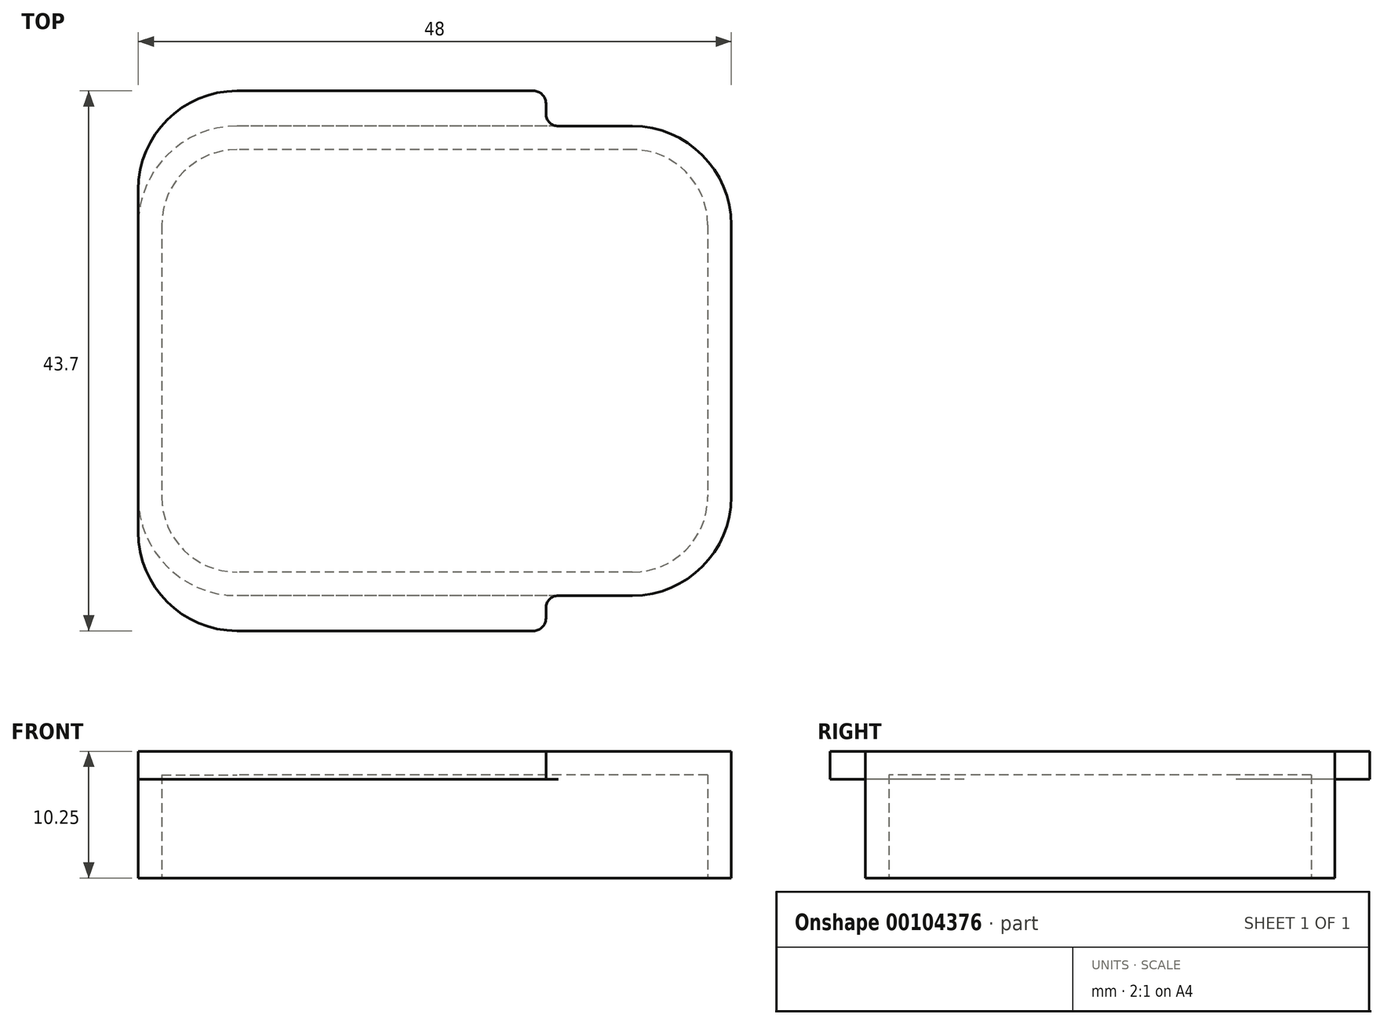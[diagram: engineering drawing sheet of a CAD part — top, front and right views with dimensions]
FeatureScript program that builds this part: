
annotation { "Feature Type Name" : "Feature", "Feature Type Description" : "" }
export const myFeature = defineFeature(function(context is Context, id is Id, definition is map)
    precondition{}
    {
        {
            var Q0;
            Q0=qCreatedBy(makeId("Top.planeOp"),FACE);
            var sketch = newSketch(context, id + "F0", { "sketchPlane" : qUnion([Q0])});
            skLineSegment(sketch, "E0.bottom", {"start": v(16, 19) * mm, "end": v(-16, 19) * mm});
            skLineSegment(sketch, "E0.top", {"start": v(16, -19) * mm, "end": v(-16, -19) * mm});
            skLineSegment(sketch, "E0.left", {"start": v(24, 11) * mm, "end": v(24, -11) * mm});
            skLineSegment(sketch, "E0.right", {"start": v(-24, 11) * mm, "end": v(-24, -11) * mm});
            skPoint(sketch, "E0.middle", {"position": v(0, 0) * mm});
            skPoint(sketch, "E1.visualSharp", {"position": v(24, 19) * mm});
            skArc(sketch, "E1.filletArc", {"start": v(24, 11) * mm, "mid": v(21.66, 16.66) * mm, "end": v(16, 19) * mm});
            skPoint(sketch, "E2.visualSharp", {"position": v(-24, 19) * mm});
            skArc(sketch, "E2.filletArc", {"start": v(-16, 19) * mm, "mid": v(-21.66, 16.66) * mm, "end": v(-24, 11) * mm});
            skPoint(sketch, "E3.visualSharp", {"position": v(-24, -19) * mm});
            skArc(sketch, "E3.filletArc", {"start": v(-24, -11) * mm, "mid": v(-21.66, -16.66) * mm, "end": v(-16, -19) * mm});
            skPoint(sketch, "E4.visualSharp", {"position": v(24, -19) * mm});
            skArc(sketch, "E4.filletArc", {"start": v(16, -19) * mm, "mid": v(21.66, -16.66) * mm, "end": v(24, -11) * mm});
            skSolve(sketch);
        }
        {
            var Q0;
            Q0=makeQuery(id+"F0.imprint","IMPRINT",FACE,{"disambiguationData":[TD([[makeQuery(id+"F0.imprint","IMPRINT",EDGE,{"derivedFrom":sQuery(id+"F0.wireOp",EDGE,"E0.bottom")}),1.0]])]});
            extrude(context, id + "F1", {"entities" : qUnion([Q0]), "depth" : 10.25 * mm});
        }
        {
            var Q0;
            Q0=makeQuery(id+"F1.opExtrude","CAP_FACE",FACE,{"disambiguationData":[OSD([sQuery(id+"F0.wireOp",EDGE,"E0.bottom"),sQuery(id+"F0.wireOp",EDGE,"E0.top"),sQuery(id+"F0.wireOp",EDGE,"E0.left"),sQuery(id+"F0.wireOp",EDGE,"E0.right"),sQuery(id+"F0.wireOp",EDGE,"E1.filletArc"),sQuery(id+"F0.wireOp",EDGE,"E2.filletArc"),sQuery(id+"F0.wireOp",EDGE,"E3.filletArc"),sQuery(id+"F0.wireOp",EDGE,"E4.filletArc")])],"isStart":false});
            var sketch = newSketch(context, id + "F2", { "sketchPlane" : qUnion([Q0])});
            skLineSegment(sketch, "E5.bottom", {"start": v(-16, 21.85) * mm, "end": v(8, 21.85) * mm});
            skLineSegment(sketch, "E5.top", {"start": v(-16, -21.85) * mm, "end": v(8, -21.85) * mm});
            skLineSegment(sketch, "E5.left", {"start": v(-24, 13.85) * mm, "end": v(-24, -13.85) * mm});
            skLineSegment(sketch, "E5.right", {"start": v(9, 20.85) * mm, "end": v(9, -20.85) * mm});
            skPoint(sketch, "E6.visualSharp", {"position": v(-24, 21.85) * mm});
            skArc(sketch, "E6.filletArc", {"start": v(-16, 21.85) * mm, "mid": v(-21.66, 19.5) * mm, "end": v(-24, 13.85) * mm});
            skPoint(sketch, "E7.visualSharp", {"position": v(-24, -21.85) * mm});
            skArc(sketch, "E7.filletArc", {"start": v(-24, -13.85) * mm, "mid": v(-21.66, -19.5) * mm, "end": v(-16, -21.85) * mm});
            skPoint(sketch, "E8.visualSharp", {"position": v(9, -21.85) * mm});
            skArc(sketch, "E8.filletArc", {"start": v(8, -21.85) * mm, "mid": v(8.7, -21.56) * mm, "end": v(9, -20.85) * mm});
            skPoint(sketch, "E9.visualSharp", {"position": v(9, 21.85) * mm});
            skArc(sketch, "E9.filletArc", {"start": v(9, 20.85) * mm, "mid": v(8.7, 21.56) * mm, "end": v(8, 21.85) * mm});
            skSolve(sketch);
        }
        {
            var Q0;
            Q0 = qSketchRegion(id + "F2", true);
            extrude(context, id + "F3", {"entities" : qUnion([Q0]), "operationType" : NewBodyOperationType.ADD, "oppositeDirection" : true, "depth" : 2.25 * mm});
        }
        {
            var Q0;
            Q0=makeQuery(id+"F3.boolean.opBoolean","INTERSECT",EDGE,{"derivedFrom":[makeQuery(id+"F1.opExtrude","SWEPT_FACE",FACE,{"disambiguationData":[OSD([sQuery(id+"F0.wireOp",EDGE,"E0.top")])]}),makeQuery(id+"F3.opExtrude","SWEPT_FACE",FACE,{"disambiguationData":[OSD([sQuery(id+"F2.wireOp",EDGE,"E5.right")])]})]});
            var Q1;
            Q1=makeQuery(id+"F3.boolean.opBoolean","INTERSECT",EDGE,{"derivedFrom":[makeQuery(id+"F1.opExtrude","SWEPT_FACE",FACE,{"disambiguationData":[OSD([sQuery(id+"F0.wireOp",EDGE,"E0.bottom")])]}),makeQuery(id+"F3.opExtrude","SWEPT_FACE",FACE,{"disambiguationData":[OSD([sQuery(id+"F2.wireOp",EDGE,"E5.right")])]})]});
            fillet(context, id + "F4", {"entities" : qUnion([Q0, Q1]), "radius" : 1 * mm, "tangentPropagation" : true, "allowEdgeOverflow" : false});
        }
        {
            var Q0;
            Q0=makeQuery(id+"F1.opExtrude","CAP_FACE",FACE,{"disambiguationData":[OSD([sQuery(id+"F0.wireOp",EDGE,"E0.bottom"),sQuery(id+"F0.wireOp",EDGE,"E0.top"),sQuery(id+"F0.wireOp",EDGE,"E0.left"),sQuery(id+"F0.wireOp",EDGE,"E0.right"),sQuery(id+"F0.wireOp",EDGE,"E1.filletArc"),sQuery(id+"F0.wireOp",EDGE,"E2.filletArc"),sQuery(id+"F0.wireOp",EDGE,"E3.filletArc"),sQuery(id+"F0.wireOp",EDGE,"E4.filletArc")])],"isStart":true});
            shell(context, id + "F5", {"entities" : qUnion([Q0]), "thickness" : 1.9 * mm});
        }
    });
